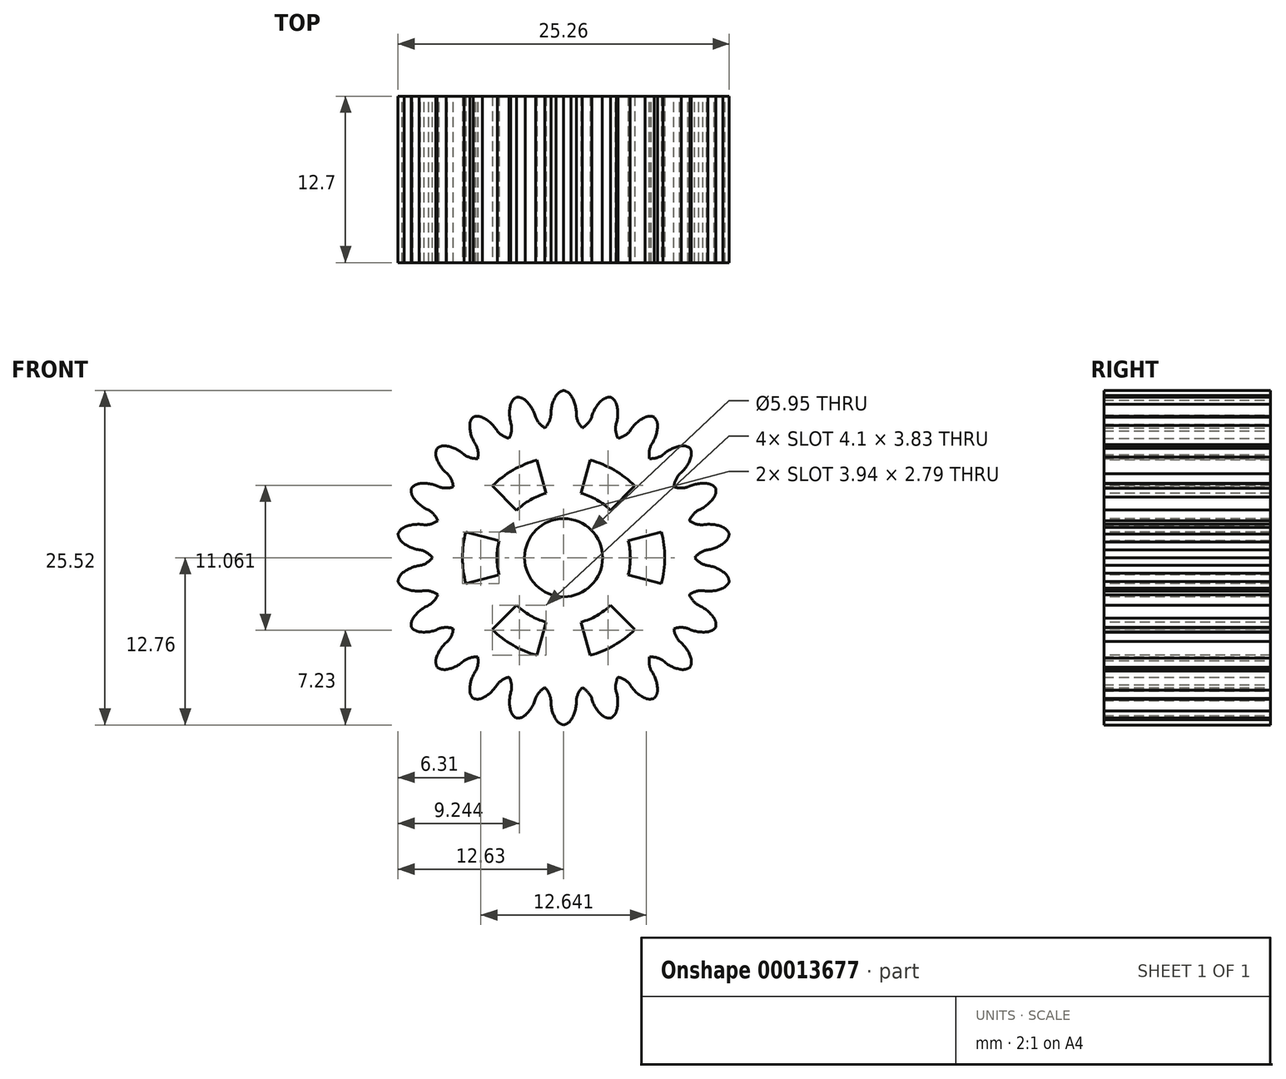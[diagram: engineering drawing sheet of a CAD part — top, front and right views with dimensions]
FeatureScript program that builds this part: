
annotation { "Feature Type Name" : "Feature", "Feature Type Description" : "" }
export const myFeature = defineFeature(function(context is Context, id is Id, definition is map)
    precondition{}
    {
        {
            var Q0;
            Q0=qCreatedBy(makeId("Front.planeOp"),FACE);
            var sketch = newSketch(context, id + "F0", { "sketchPlane" : qUnion([Q0])});
            skLineSegment(sketch, "E0", {"start": v(0, 0) * mm, "end": v(0, 16.94) * mm});
            skArc(sketch, "E1", {"start": v(0, 12.76) * mm, "mid": v(-0.32, 12.62) * mm, "end": v(-0.57, 12.37) * mm});
            skArc(sketch, "E2.MirrorCS", {"start": v(0, 12.76) * mm, "mid": v(0.32, 12.62) * mm, "end": v(0.57, 12.37) * mm});
            skArc(sketch, "E3", {"start": v(-0.57, 12.37) * mm, "mid": v(-0.88, 11.66) * mm, "end": v(-0.97, 10.89) * mm});
            skArc(sketch, "E4", {"start": v(-1.42, 9.9) * mm, "mid": v(-1.11, 10.36) * mm, "end": v(-0.97, 10.89) * mm});
            skArc(sketch, "E5.MirrorCS", {"start": v(1.42, 9.9) * mm, "mid": v(1.11, 10.36) * mm, "end": v(0.97, 10.89) * mm});
            skArc(sketch, "E6.MirrorCS", {"start": v(0.57, 12.37) * mm, "mid": v(0.88, 11.66) * mm, "end": v(0.97, 10.89) * mm});
            skPoint(sketch, "E7", {"position": v(0, 12.7) * mm});
            skPoint(sketch, "E8.MirrorCS.end.orphan", {"position": v(0.57, 12.37) * mm});
            skPoint(sketch, "E8.MirrorCS.start.orphan", {"position": v(0, 12.37) * mm});
            skPoint(sketch, "E9.1.0", {"position": v(-3.48, 11.87) * mm});
            skPoint(sketch, "E9.1.1", {"position": v(-2.94, 12.03) * mm});
            skArc(sketch, "E9.1.2", {"start": v(-2.94, 12.03) * mm, "mid": v(-2.44, 11.43) * mm, "end": v(-2.14, 10.72) * mm});
            skPoint(sketch, "E9.1.3", {"position": v(-3.58, 12.19) * mm});
            skArc(sketch, "E9.1.4", {"start": v(-4.03, 11.7) * mm, "mid": v(-4.13, 10.94) * mm, "end": v(-4, 10.17) * mm});
            skArc(sketch, "E9.1.5", {"start": v(-4.16, 9.1) * mm, "mid": v(-3.99, 9.62) * mm, "end": v(-4, 10.17) * mm});
            skArc(sketch, "E9.1.6", {"start": v(-1.42, 9.9) * mm, "mid": v(-1.85, 10.25) * mm, "end": v(-2.14, 10.72) * mm});
            skPoint(sketch, "E9.1.7", {"position": v(-3.48, 11.87) * mm});
            skArc(sketch, "E9.1.8", {"start": v(-3.6, 12.25) * mm, "mid": v(-3.87, 12.02) * mm, "end": v(-4.03, 11.7) * mm});
            skArc(sketch, "E9.1.9", {"start": v(-3.6, 12.25) * mm, "mid": v(-3.25, 12.2) * mm, "end": v(-2.94, 12.03) * mm});
            skPoint(sketch, "E9.2.0", {"position": v(-6.69, 10.4) * mm});
            skPoint(sketch, "E9.2.1", {"position": v(-6.2, 10.71) * mm});
            skArc(sketch, "E9.2.2", {"start": v(-6.2, 10.71) * mm, "mid": v(-5.56, 10.28) * mm, "end": v(-5.07, 9.68) * mm});
            skPoint(sketch, "E9.2.3", {"position": v(-6.87, 10.68) * mm});
            skArc(sketch, "E9.2.4", {"start": v(-7.17, 10.1) * mm, "mid": v(-7.04, 9.33) * mm, "end": v(-6.7, 8.63) * mm});
            skArc(sketch, "E9.2.5", {"start": v(-6.55, 7.56) * mm, "mid": v(-6.54, 8.11) * mm, "end": v(-6.7, 8.63) * mm});
            skArc(sketch, "E9.2.6", {"start": v(-4.16, 9.1) * mm, "mid": v(-4.66, 9.32) * mm, "end": v(-5.07, 9.68) * mm});
            skPoint(sketch, "E9.2.7", {"position": v(-6.69, 10.4) * mm});
            skArc(sketch, "E9.2.8", {"start": v(-6.9, 10.74) * mm, "mid": v(-7.1, 10.44) * mm, "end": v(-7.17, 10.1) * mm});
            skArc(sketch, "E9.2.9", {"start": v(-6.9, 10.74) * mm, "mid": v(-6.55, 10.8) * mm, "end": v(-6.2, 10.71) * mm});
            skPoint(sketch, "E9.3.0", {"position": v(-9.35, 8.1) * mm});
            skPoint(sketch, "E9.3.1", {"position": v(-8.97, 8.53) * mm});
            skArc(sketch, "E9.3.2", {"start": v(-8.97, 8.53) * mm, "mid": v(-8.23, 8.3) * mm, "end": v(-7.6, 7.86) * mm});
            skPoint(sketch, "E9.3.3", {"position": v(-9.6, 8.32) * mm});
            skArc(sketch, "E9.3.4", {"start": v(-9.72, 7.67) * mm, "mid": v(-9.39, 6.97) * mm, "end": v(-8.86, 6.4) * mm});
            skArc(sketch, "E9.3.5", {"start": v(-8.42, 5.41) * mm, "mid": v(-8.56, 5.94) * mm, "end": v(-8.86, 6.4) * mm});
            skArc(sketch, "E9.3.6", {"start": v(-6.55, 7.56) * mm, "mid": v(-7.1, 7.62) * mm, "end": v(-7.6, 7.86) * mm});
            skPoint(sketch, "E9.3.7", {"position": v(-9.35, 8.1) * mm});
            skArc(sketch, "E9.3.8", {"start": v(-9.65, 8.36) * mm, "mid": v(-9.75, 8.02) * mm, "end": v(-9.72, 7.67) * mm});
            skArc(sketch, "E9.3.9", {"start": v(-9.65, 8.36) * mm, "mid": v(-9.33, 8.5) * mm, "end": v(-8.97, 8.53) * mm});
            skPoint(sketch, "E9.4.0", {"position": v(-11.25, 5.14) * mm});
            skPoint(sketch, "E9.4.1", {"position": v(-11.01, 5.66) * mm});
            skArc(sketch, "E9.4.2", {"start": v(-11.01, 5.66) * mm, "mid": v(-10.24, 5.64) * mm, "end": v(-9.5, 5.4) * mm});
            skPoint(sketch, "E9.4.3", {"position": v(-11.55, 5.28) * mm});
            skArc(sketch, "E9.4.4", {"start": v(-11.49, 4.62) * mm, "mid": v(-10.97, 4.04) * mm, "end": v(-10.3, 3.64) * mm});
            skArc(sketch, "E9.4.5", {"start": v(-9.6, 2.82) * mm, "mid": v(-9.88, 3.3) * mm, "end": v(-10.3, 3.64) * mm});
            skArc(sketch, "E9.4.6", {"start": v(-8.42, 5.41) * mm, "mid": v(-8.96, 5.32) * mm, "end": v(-9.5, 5.4) * mm});
            skPoint(sketch, "E9.4.7", {"position": v(-11.25, 5.14) * mm});
            skArc(sketch, "E9.4.8", {"start": v(-11.6, 5.3) * mm, "mid": v(-11.61, 4.95) * mm, "end": v(-11.49, 4.62) * mm});
            skArc(sketch, "E9.4.9", {"start": v(-11.6, 5.3) * mm, "mid": v(-11.35, 5.54) * mm, "end": v(-11.01, 5.66) * mm});
            skPoint(sketch, "E9.5.0", {"position": v(-12.24, 1.76) * mm});
            skPoint(sketch, "E9.5.1", {"position": v(-12.16, 2.32) * mm});
            skArc(sketch, "E9.5.2", {"start": v(-12.16, 2.32) * mm, "mid": v(-11.41, 2.53) * mm, "end": v(-10.64, 2.5) * mm});
            skPoint(sketch, "E9.5.3", {"position": v(-12.57, 1.8) * mm});
            skArc(sketch, "E9.5.4", {"start": v(-12.32, 1.2) * mm, "mid": v(-11.66, 0.79) * mm, "end": v(-10.91, 0.59) * mm});
            skArc(sketch, "E9.5.5", {"start": v(-10, 0) * mm, "mid": v(-10.41, 0.37) * mm, "end": v(-10.91, 0.59) * mm});
            skArc(sketch, "E9.5.6", {"start": v(-9.6, 2.82) * mm, "mid": v(-10.1, 2.58) * mm, "end": v(-10.64, 2.5) * mm});
            skPoint(sketch, "E9.5.7", {"position": v(-12.24, 1.76) * mm});
            skArc(sketch, "E9.5.8", {"start": v(-12.63, 1.82) * mm, "mid": v(-12.54, 1.48) * mm, "end": v(-12.32, 1.2) * mm});
            skArc(sketch, "E9.5.9", {"start": v(-12.63, 1.82) * mm, "mid": v(-12.45, 2.12) * mm, "end": v(-12.16, 2.32) * mm});
            skPoint(sketch, "E9.6.0", {"position": v(-12.24, -1.76) * mm});
            skPoint(sketch, "E9.6.1", {"position": v(-12.32, -1.2) * mm});
            skArc(sketch, "E9.6.2", {"start": v(-12.32, -1.2) * mm, "mid": v(-11.66, -0.79) * mm, "end": v(-10.91, -0.59) * mm});
            skPoint(sketch, "E9.6.3", {"position": v(-12.57, -1.8) * mm});
            skArc(sketch, "E9.6.4", {"start": v(-12.16, -2.32) * mm, "mid": v(-11.41, -2.53) * mm, "end": v(-10.64, -2.5) * mm});
            skArc(sketch, "E9.6.5", {"start": v(-9.6, -2.82) * mm, "mid": v(-10.1, -2.58) * mm, "end": v(-10.64, -2.5) * mm});
            skArc(sketch, "E9.6.6", {"start": v(-10, 0) * mm, "mid": v(-10.41, -0.37) * mm, "end": v(-10.91, -0.59) * mm});
            skPoint(sketch, "E9.6.7", {"position": v(-12.24, -1.76) * mm});
            skArc(sketch, "E9.6.8", {"start": v(-12.63, -1.82) * mm, "mid": v(-12.45, -2.12) * mm, "end": v(-12.16, -2.32) * mm});
            skArc(sketch, "E9.6.9", {"start": v(-12.63, -1.82) * mm, "mid": v(-12.54, -1.48) * mm, "end": v(-12.32, -1.2) * mm});
            skPoint(sketch, "E9.7.0", {"position": v(-11.25, -5.14) * mm});
            skPoint(sketch, "E9.7.1", {"position": v(-11.49, -4.62) * mm});
            skArc(sketch, "E9.7.2", {"start": v(-11.49, -4.62) * mm, "mid": v(-10.97, -4.04) * mm, "end": v(-10.3, -3.64) * mm});
            skPoint(sketch, "E9.7.3", {"position": v(-11.55, -5.28) * mm});
            skArc(sketch, "E9.7.4", {"start": v(-11.01, -5.66) * mm, "mid": v(-10.24, -5.64) * mm, "end": v(-9.5, -5.4) * mm});
            skArc(sketch, "E9.7.5", {"start": v(-8.42, -5.41) * mm, "mid": v(-8.96, -5.32) * mm, "end": v(-9.5, -5.4) * mm});
            skArc(sketch, "E9.7.6", {"start": v(-9.6, -2.82) * mm, "mid": v(-9.88, -3.3) * mm, "end": v(-10.3, -3.64) * mm});
            skPoint(sketch, "E9.7.7", {"position": v(-11.25, -5.14) * mm});
            skArc(sketch, "E9.7.8", {"start": v(-11.6, -5.3) * mm, "mid": v(-11.35, -5.54) * mm, "end": v(-11.01, -5.66) * mm});
            skArc(sketch, "E9.7.9", {"start": v(-11.6, -5.3) * mm, "mid": v(-11.61, -4.95) * mm, "end": v(-11.49, -4.62) * mm});
            skPoint(sketch, "E9.8.0", {"position": v(-9.35, -8.1) * mm});
            skPoint(sketch, "E9.8.1", {"position": v(-9.72, -7.67) * mm});
            skArc(sketch, "E9.8.2", {"start": v(-9.72, -7.67) * mm, "mid": v(-9.39, -6.97) * mm, "end": v(-8.86, -6.4) * mm});
            skPoint(sketch, "E9.8.3", {"position": v(-9.6, -8.32) * mm});
            skArc(sketch, "E9.8.4", {"start": v(-8.97, -8.53) * mm, "mid": v(-8.23, -8.3) * mm, "end": v(-7.6, -7.86) * mm});
            skArc(sketch, "E9.8.5", {"start": v(-6.55, -7.56) * mm, "mid": v(-7.1, -7.62) * mm, "end": v(-7.6, -7.86) * mm});
            skArc(sketch, "E9.8.6", {"start": v(-8.42, -5.41) * mm, "mid": v(-8.56, -5.94) * mm, "end": v(-8.86, -6.4) * mm});
            skPoint(sketch, "E9.8.7", {"position": v(-9.35, -8.1) * mm});
            skArc(sketch, "E9.8.8", {"start": v(-9.65, -8.36) * mm, "mid": v(-9.33, -8.5) * mm, "end": v(-8.97, -8.53) * mm});
            skArc(sketch, "E9.8.9", {"start": v(-9.65, -8.36) * mm, "mid": v(-9.75, -8.02) * mm, "end": v(-9.72, -7.67) * mm});
            skPoint(sketch, "E9.9.0", {"position": v(-6.69, -10.4) * mm});
            skPoint(sketch, "E9.9.1", {"position": v(-7.17, -10.1) * mm});
            skArc(sketch, "E9.9.2", {"start": v(-7.17, -10.1) * mm, "mid": v(-7.04, -9.33) * mm, "end": v(-6.7, -8.63) * mm});
            skPoint(sketch, "E9.9.3", {"position": v(-6.87, -10.68) * mm});
            skArc(sketch, "E9.9.4", {"start": v(-6.2, -10.71) * mm, "mid": v(-5.56, -10.28) * mm, "end": v(-5.07, -9.68) * mm});
            skArc(sketch, "E9.9.5", {"start": v(-4.16, -9.1) * mm, "mid": v(-4.66, -9.32) * mm, "end": v(-5.07, -9.68) * mm});
            skArc(sketch, "E9.9.6", {"start": v(-6.55, -7.56) * mm, "mid": v(-6.54, -8.11) * mm, "end": v(-6.7, -8.63) * mm});
            skPoint(sketch, "E9.9.7", {"position": v(-6.69, -10.4) * mm});
            skArc(sketch, "E9.9.8", {"start": v(-6.9, -10.74) * mm, "mid": v(-6.55, -10.8) * mm, "end": v(-6.2, -10.71) * mm});
            skArc(sketch, "E9.9.9", {"start": v(-6.9, -10.74) * mm, "mid": v(-7.1, -10.44) * mm, "end": v(-7.17, -10.1) * mm});
            skPoint(sketch, "E9.10.0", {"position": v(-3.48, -11.87) * mm});
            skPoint(sketch, "E9.10.1", {"position": v(-4.03, -11.7) * mm});
            skArc(sketch, "E9.10.2", {"start": v(-4.03, -11.7) * mm, "mid": v(-4.13, -10.94) * mm, "end": v(-4, -10.17) * mm});
            skPoint(sketch, "E9.10.3", {"position": v(-3.58, -12.19) * mm});
            skArc(sketch, "E9.10.4", {"start": v(-2.94, -12.03) * mm, "mid": v(-2.44, -11.43) * mm, "end": v(-2.14, -10.72) * mm});
            skArc(sketch, "E9.10.5", {"start": v(-1.42, -9.9) * mm, "mid": v(-1.85, -10.25) * mm, "end": v(-2.14, -10.72) * mm});
            skArc(sketch, "E9.10.6", {"start": v(-4.16, -9.1) * mm, "mid": v(-3.99, -9.62) * mm, "end": v(-4, -10.17) * mm});
            skPoint(sketch, "E9.10.7", {"position": v(-3.48, -11.87) * mm});
            skArc(sketch, "E9.10.8", {"start": v(-3.6, -12.25) * mm, "mid": v(-3.25, -12.2) * mm, "end": v(-2.94, -12.03) * mm});
            skArc(sketch, "E9.10.9", {"start": v(-3.6, -12.25) * mm, "mid": v(-3.87, -12.02) * mm, "end": v(-4.03, -11.7) * mm});
            skPoint(sketch, "E9.11.0", {"position": v(0, -12.37) * mm});
            skPoint(sketch, "E9.11.1", {"position": v(-0.57, -12.37) * mm});
            skArc(sketch, "E9.11.2", {"start": v(-0.57, -12.37) * mm, "mid": v(-0.88, -11.66) * mm, "end": v(-0.97, -10.89) * mm});
            skPoint(sketch, "E9.11.3", {"position": v(0, -12.7) * mm});
            skArc(sketch, "E9.11.4", {"start": v(0.57, -12.37) * mm, "mid": v(0.88, -11.66) * mm, "end": v(0.97, -10.89) * mm});
            skArc(sketch, "E9.11.5", {"start": v(1.42, -9.9) * mm, "mid": v(1.11, -10.36) * mm, "end": v(0.97, -10.89) * mm});
            skArc(sketch, "E9.11.6", {"start": v(-1.42, -9.9) * mm, "mid": v(-1.11, -10.36) * mm, "end": v(-0.97, -10.89) * mm});
            skPoint(sketch, "E9.11.7", {"position": v(0, -12.37) * mm});
            skArc(sketch, "E9.11.8", {"start": v(0, -12.76) * mm, "mid": v(0.32, -12.62) * mm, "end": v(0.57, -12.37) * mm});
            skArc(sketch, "E9.11.9", {"start": v(0, -12.76) * mm, "mid": v(-0.32, -12.62) * mm, "end": v(-0.57, -12.37) * mm});
            skPoint(sketch, "E9.12.0", {"position": v(3.48, -11.87) * mm});
            skPoint(sketch, "E9.12.1", {"position": v(2.94, -12.03) * mm});
            skArc(sketch, "E9.12.2", {"start": v(2.94, -12.03) * mm, "mid": v(2.44, -11.43) * mm, "end": v(2.14, -10.72) * mm});
            skPoint(sketch, "E9.12.3", {"position": v(3.58, -12.19) * mm});
            skArc(sketch, "E9.12.4", {"start": v(4.03, -11.7) * mm, "mid": v(4.13, -10.94) * mm, "end": v(4, -10.17) * mm});
            skArc(sketch, "E9.12.5", {"start": v(4.16, -9.1) * mm, "mid": v(3.99, -9.62) * mm, "end": v(4, -10.17) * mm});
            skArc(sketch, "E9.12.6", {"start": v(1.42, -9.9) * mm, "mid": v(1.85, -10.25) * mm, "end": v(2.14, -10.72) * mm});
            skPoint(sketch, "E9.12.7", {"position": v(3.48, -11.87) * mm});
            skArc(sketch, "E9.12.8", {"start": v(3.6, -12.25) * mm, "mid": v(3.87, -12.02) * mm, "end": v(4.03, -11.7) * mm});
            skArc(sketch, "E9.12.9", {"start": v(3.6, -12.25) * mm, "mid": v(3.25, -12.2) * mm, "end": v(2.94, -12.03) * mm});
            skPoint(sketch, "E9.13.0", {"position": v(6.69, -10.4) * mm});
            skPoint(sketch, "E9.13.1", {"position": v(6.2, -10.71) * mm});
            skArc(sketch, "E9.13.2", {"start": v(6.2, -10.71) * mm, "mid": v(5.56, -10.28) * mm, "end": v(5.07, -9.68) * mm});
            skPoint(sketch, "E9.13.3", {"position": v(6.87, -10.68) * mm});
            skArc(sketch, "E9.13.4", {"start": v(7.17, -10.1) * mm, "mid": v(7.04, -9.33) * mm, "end": v(6.7, -8.63) * mm});
            skArc(sketch, "E9.13.5", {"start": v(6.55, -7.56) * mm, "mid": v(6.54, -8.11) * mm, "end": v(6.7, -8.63) * mm});
            skArc(sketch, "E9.13.6", {"start": v(4.16, -9.1) * mm, "mid": v(4.66, -9.32) * mm, "end": v(5.07, -9.68) * mm});
            skPoint(sketch, "E9.13.7", {"position": v(6.69, -10.4) * mm});
            skArc(sketch, "E9.13.8", {"start": v(6.9, -10.74) * mm, "mid": v(7.1, -10.44) * mm, "end": v(7.17, -10.1) * mm});
            skArc(sketch, "E9.13.9", {"start": v(6.9, -10.74) * mm, "mid": v(6.55, -10.8) * mm, "end": v(6.2, -10.71) * mm});
            skPoint(sketch, "E9.14.0", {"position": v(9.35, -8.1) * mm});
            skPoint(sketch, "E9.14.1", {"position": v(8.97, -8.53) * mm});
            skArc(sketch, "E9.14.2", {"start": v(8.97, -8.53) * mm, "mid": v(8.23, -8.3) * mm, "end": v(7.6, -7.86) * mm});
            skPoint(sketch, "E9.14.3", {"position": v(9.6, -8.32) * mm});
            skArc(sketch, "E9.14.4", {"start": v(9.72, -7.67) * mm, "mid": v(9.39, -6.97) * mm, "end": v(8.86, -6.4) * mm});
            skArc(sketch, "E9.14.5", {"start": v(8.42, -5.41) * mm, "mid": v(8.56, -5.94) * mm, "end": v(8.86, -6.4) * mm});
            skArc(sketch, "E9.14.6", {"start": v(6.55, -7.56) * mm, "mid": v(7.1, -7.62) * mm, "end": v(7.6, -7.86) * mm});
            skPoint(sketch, "E9.14.7", {"position": v(9.35, -8.1) * mm});
            skArc(sketch, "E9.14.8", {"start": v(9.65, -8.36) * mm, "mid": v(9.75, -8.02) * mm, "end": v(9.72, -7.67) * mm});
            skArc(sketch, "E9.14.9", {"start": v(9.65, -8.36) * mm, "mid": v(9.33, -8.5) * mm, "end": v(8.97, -8.53) * mm});
            skPoint(sketch, "E9.15.0", {"position": v(11.25, -5.14) * mm});
            skPoint(sketch, "E9.15.1", {"position": v(11.01, -5.66) * mm});
            skArc(sketch, "E9.15.2", {"start": v(11.01, -5.66) * mm, "mid": v(10.24, -5.64) * mm, "end": v(9.5, -5.4) * mm});
            skPoint(sketch, "E9.15.3", {"position": v(11.55, -5.28) * mm});
            skArc(sketch, "E9.15.4", {"start": v(11.49, -4.62) * mm, "mid": v(10.97, -4.04) * mm, "end": v(10.3, -3.64) * mm});
            skArc(sketch, "E9.15.5", {"start": v(9.6, -2.82) * mm, "mid": v(9.88, -3.3) * mm, "end": v(10.3, -3.64) * mm});
            skArc(sketch, "E9.15.6", {"start": v(8.42, -5.41) * mm, "mid": v(8.96, -5.32) * mm, "end": v(9.5, -5.4) * mm});
            skPoint(sketch, "E9.15.7", {"position": v(11.25, -5.14) * mm});
            skArc(sketch, "E9.15.8", {"start": v(11.6, -5.3) * mm, "mid": v(11.61, -4.95) * mm, "end": v(11.49, -4.62) * mm});
            skArc(sketch, "E9.15.9", {"start": v(11.6, -5.3) * mm, "mid": v(11.35, -5.54) * mm, "end": v(11.01, -5.66) * mm});
            skPoint(sketch, "E9.16.0", {"position": v(12.24, -1.76) * mm});
            skPoint(sketch, "E9.16.1", {"position": v(12.16, -2.32) * mm});
            skArc(sketch, "E9.16.2", {"start": v(12.16, -2.32) * mm, "mid": v(11.41, -2.53) * mm, "end": v(10.64, -2.5) * mm});
            skPoint(sketch, "E9.16.3", {"position": v(12.57, -1.8) * mm});
            skArc(sketch, "E9.16.4", {"start": v(12.32, -1.2) * mm, "mid": v(11.66, -0.79) * mm, "end": v(10.91, -0.59) * mm});
            skArc(sketch, "E9.16.5", {"start": v(10, 0) * mm, "mid": v(10.41, -0.37) * mm, "end": v(10.91, -0.59) * mm});
            skArc(sketch, "E9.16.6", {"start": v(9.6, -2.82) * mm, "mid": v(10.1, -2.58) * mm, "end": v(10.64, -2.5) * mm});
            skPoint(sketch, "E9.16.7", {"position": v(12.24, -1.76) * mm});
            skArc(sketch, "E9.16.8", {"start": v(12.63, -1.82) * mm, "mid": v(12.54, -1.48) * mm, "end": v(12.32, -1.2) * mm});
            skArc(sketch, "E9.16.9", {"start": v(12.63, -1.82) * mm, "mid": v(12.45, -2.12) * mm, "end": v(12.16, -2.32) * mm});
            skPoint(sketch, "E9.17.0", {"position": v(12.24, 1.76) * mm});
            skPoint(sketch, "E9.17.1", {"position": v(12.32, 1.2) * mm});
            skArc(sketch, "E9.17.2", {"start": v(12.32, 1.2) * mm, "mid": v(11.66, 0.79) * mm, "end": v(10.91, 0.59) * mm});
            skPoint(sketch, "E9.17.3", {"position": v(12.57, 1.8) * mm});
            skArc(sketch, "E9.17.4", {"start": v(12.16, 2.32) * mm, "mid": v(11.41, 2.53) * mm, "end": v(10.64, 2.5) * mm});
            skArc(sketch, "E9.17.5", {"start": v(9.6, 2.82) * mm, "mid": v(10.1, 2.58) * mm, "end": v(10.64, 2.5) * mm});
            skArc(sketch, "E9.17.6", {"start": v(10, 0) * mm, "mid": v(10.41, 0.37) * mm, "end": v(10.91, 0.59) * mm});
            skPoint(sketch, "E9.17.7", {"position": v(12.24, 1.76) * mm});
            skArc(sketch, "E9.17.8", {"start": v(12.63, 1.82) * mm, "mid": v(12.45, 2.12) * mm, "end": v(12.16, 2.32) * mm});
            skArc(sketch, "E9.17.9", {"start": v(12.63, 1.82) * mm, "mid": v(12.54, 1.48) * mm, "end": v(12.32, 1.2) * mm});
            skPoint(sketch, "E9.18.0", {"position": v(11.25, 5.14) * mm});
            skPoint(sketch, "E9.18.1", {"position": v(11.49, 4.62) * mm});
            skArc(sketch, "E9.18.2", {"start": v(11.49, 4.62) * mm, "mid": v(10.97, 4.04) * mm, "end": v(10.3, 3.64) * mm});
            skPoint(sketch, "E9.18.3", {"position": v(11.55, 5.28) * mm});
            skArc(sketch, "E9.18.4", {"start": v(11.01, 5.66) * mm, "mid": v(10.24, 5.64) * mm, "end": v(9.5, 5.4) * mm});
            skArc(sketch, "E9.18.5", {"start": v(8.42, 5.41) * mm, "mid": v(8.96, 5.32) * mm, "end": v(9.5, 5.4) * mm});
            skArc(sketch, "E9.18.6", {"start": v(9.6, 2.82) * mm, "mid": v(9.88, 3.3) * mm, "end": v(10.3, 3.64) * mm});
            skPoint(sketch, "E9.18.7", {"position": v(11.25, 5.14) * mm});
            skArc(sketch, "E9.18.8", {"start": v(11.6, 5.3) * mm, "mid": v(11.35, 5.54) * mm, "end": v(11.01, 5.66) * mm});
            skArc(sketch, "E9.18.9", {"start": v(11.6, 5.3) * mm, "mid": v(11.61, 4.95) * mm, "end": v(11.49, 4.62) * mm});
            skPoint(sketch, "E9.19.0", {"position": v(9.35, 8.1) * mm});
            skPoint(sketch, "E9.19.1", {"position": v(9.72, 7.67) * mm});
            skArc(sketch, "E9.19.2", {"start": v(9.72, 7.67) * mm, "mid": v(9.39, 6.97) * mm, "end": v(8.86, 6.4) * mm});
            skPoint(sketch, "E9.19.3", {"position": v(9.6, 8.32) * mm});
            skArc(sketch, "E9.19.4", {"start": v(8.97, 8.53) * mm, "mid": v(8.23, 8.3) * mm, "end": v(7.6, 7.86) * mm});
            skArc(sketch, "E9.19.5", {"start": v(6.55, 7.56) * mm, "mid": v(7.1, 7.62) * mm, "end": v(7.6, 7.86) * mm});
            skArc(sketch, "E9.19.6", {"start": v(8.42, 5.41) * mm, "mid": v(8.56, 5.94) * mm, "end": v(8.86, 6.4) * mm});
            skPoint(sketch, "E9.19.7", {"position": v(9.35, 8.1) * mm});
            skArc(sketch, "E9.19.8", {"start": v(9.65, 8.36) * mm, "mid": v(9.33, 8.5) * mm, "end": v(8.97, 8.53) * mm});
            skArc(sketch, "E9.19.9", {"start": v(9.65, 8.36) * mm, "mid": v(9.75, 8.02) * mm, "end": v(9.72, 7.67) * mm});
            skPoint(sketch, "E9.20.0", {"position": v(6.69, 10.4) * mm});
            skPoint(sketch, "E9.20.1", {"position": v(7.17, 10.1) * mm});
            skArc(sketch, "E9.20.2", {"start": v(7.17, 10.1) * mm, "mid": v(7.04, 9.33) * mm, "end": v(6.7, 8.63) * mm});
            skPoint(sketch, "E9.20.3", {"position": v(6.87, 10.68) * mm});
            skArc(sketch, "E9.20.4", {"start": v(6.2, 10.71) * mm, "mid": v(5.56, 10.28) * mm, "end": v(5.07, 9.68) * mm});
            skArc(sketch, "E9.20.5", {"start": v(4.16, 9.1) * mm, "mid": v(4.66, 9.32) * mm, "end": v(5.07, 9.68) * mm});
            skArc(sketch, "E9.20.6", {"start": v(6.55, 7.56) * mm, "mid": v(6.54, 8.11) * mm, "end": v(6.7, 8.63) * mm});
            skPoint(sketch, "E9.20.7", {"position": v(6.69, 10.4) * mm});
            skArc(sketch, "E9.20.8", {"start": v(6.9, 10.74) * mm, "mid": v(6.55, 10.8) * mm, "end": v(6.2, 10.71) * mm});
            skArc(sketch, "E9.20.9", {"start": v(6.9, 10.74) * mm, "mid": v(7.1, 10.44) * mm, "end": v(7.17, 10.1) * mm});
            skPoint(sketch, "E9.21.0", {"position": v(3.48, 11.87) * mm});
            skPoint(sketch, "E9.21.1", {"position": v(4.03, 11.7) * mm});
            skArc(sketch, "E9.21.2", {"start": v(4.03, 11.7) * mm, "mid": v(4.13, 10.94) * mm, "end": v(4, 10.17) * mm});
            skPoint(sketch, "E9.21.3", {"position": v(3.58, 12.19) * mm});
            skArc(sketch, "E9.21.4", {"start": v(2.94, 12.03) * mm, "mid": v(2.44, 11.43) * mm, "end": v(2.14, 10.72) * mm});
            skArc(sketch, "E9.21.5", {"start": v(1.42, 9.9) * mm, "mid": v(1.85, 10.25) * mm, "end": v(2.14, 10.72) * mm});
            skArc(sketch, "E9.21.6", {"start": v(4.16, 9.1) * mm, "mid": v(3.99, 9.62) * mm, "end": v(4, 10.17) * mm});
            skPoint(sketch, "E9.21.7", {"position": v(3.48, 11.87) * mm});
            skArc(sketch, "E9.21.8", {"start": v(3.6, 12.25) * mm, "mid": v(3.25, 12.2) * mm, "end": v(2.94, 12.03) * mm});
            skArc(sketch, "E9.21.9", {"start": v(3.6, 12.25) * mm, "mid": v(3.87, 12.02) * mm, "end": v(4.03, 11.7) * mm});
            skPoint(sketch, "E9.center", {"position": v(0, 0) * mm});
            skPoint(sketch, "E10.orphan", {"position": v(-1.54, 9.8) * mm});
            skPoint(sketch, "E11.orphan", {"position": v(-1.29, 9.84) * mm});
            skPoint(sketch, "E12.orphan", {"position": v(1.54, 9.8) * mm});
            skPoint(sketch, "E13.orphan", {"position": v(1.29, 9.84) * mm});
            skPoint(sketch, "E14.orphan", {"position": v(4, 9.08) * mm});
            skPoint(sketch, "E15.orphan", {"position": v(4.24, 8.97) * mm});
            skPoint(sketch, "E16.orphan", {"position": v(6.4, 7.58) * mm});
            skPoint(sketch, "E17.orphan", {"position": v(6.6, 7.42) * mm});
            skPoint(sketch, "E18.orphan", {"position": v(8.28, 5.47) * mm});
            skPoint(sketch, "E19.orphan", {"position": v(8.41, 5.26) * mm});
            skPoint(sketch, "E20.orphan", {"position": v(9.56, 2.67) * mm});
            skPoint(sketch, "E21.orphan", {"position": v(9.92, -0.13) * mm});
            skPoint(sketch, "E22.orphan", {"position": v(9.56, -2.67) * mm});
            skPoint(sketch, "E23.orphan", {"position": v(9.48, -2.92) * mm});
            skPoint(sketch, "E24.orphan", {"position": v(8.28, -5.47) * mm});
            skPoint(sketch, "E25.orphan", {"position": v(6.6, -7.42) * mm});
            skPoint(sketch, "E26.orphan", {"position": v(6.4, -7.58) * mm});
            skPoint(sketch, "E27.orphan", {"position": v(4.24, -8.97) * mm});
            skPoint(sketch, "E28.orphan", {"position": v(4, -9.08) * mm});
            skPoint(sketch, "E29.orphan", {"position": v(1.29, -9.84) * mm});
            skPoint(sketch, "E30.orphan", {"position": v(1.54, -9.8) * mm});
            skPoint(sketch, "E31.orphan", {"position": v(-1.29, -9.84) * mm});
            skPoint(sketch, "E32.orphan", {"position": v(-1.54, -9.8) * mm});
            skPoint(sketch, "E33.orphan", {"position": v(-4, -9.08) * mm});
            skPoint(sketch, "E34.orphan", {"position": v(-4.24, -8.97) * mm});
            skPoint(sketch, "E35.orphan", {"position": v(-6.4, -7.58) * mm});
            skPoint(sketch, "E36.orphan", {"position": v(-6.6, -7.42) * mm});
            skPoint(sketch, "E37.orphan", {"position": v(-8.41, -5.26) * mm});
            skPoint(sketch, "E38.orphan", {"position": v(-8.28, -5.47) * mm});
            skPoint(sketch, "E39.orphan", {"position": v(-9.56, -2.67) * mm});
            skPoint(sketch, "E40.orphan", {"position": v(-9.48, -2.92) * mm});
            skPoint(sketch, "E41.orphan", {"position": v(-9.92, -0.13) * mm});
            skPoint(sketch, "E42.orphan", {"position": v(-9.92, 0.13) * mm});
            skPoint(sketch, "E43.orphan", {"position": v(-9.56, 2.67) * mm});
            skPoint(sketch, "E44.orphan", {"position": v(-9.48, 2.92) * mm});
            skPoint(sketch, "E45.orphan", {"position": v(-8.41, 5.26) * mm});
            skPoint(sketch, "E46.orphan", {"position": v(-8.28, 5.47) * mm});
            skPoint(sketch, "E47.orphan", {"position": v(-6.6, 7.42) * mm});
            skPoint(sketch, "E48.orphan", {"position": v(-6.4, 7.58) * mm});
            skPoint(sketch, "E49.orphan", {"position": v(-4.24, 8.97) * mm});
            skPoint(sketch, "E50.orphan", {"position": v(-4, 9.08) * mm});
            skSolve(sketch);
        }
        {
            var Q0;
            Q0=makeQuery(id+"F0.imprint","IMPRINT",FACE,{"disambiguationData":[TD([[makeQuery(id+"F0.imprint","IMPRINT",EDGE,{"derivedFrom":sQuery(id+"F0.wireOp",EDGE,"E1")}),1.0]])]});
            extrude(context, id + "F1", {"entities" : qUnion([Q0]), "depth" : 12.7 * mm});
        }
        {
            var Q0;
            Q0=makeQuery(id+"F1.opExtrude","CAP_FACE",FACE,{"disambiguationData":[OSD([sQuery(id+"F0.wireOp",EDGE,"E1"),sQuery(id+"F0.wireOp",EDGE,"E2.MirrorCS"),sQuery(id+"F0.wireOp",EDGE,"E3"),sQuery(id+"F0.wireOp",EDGE,"E4"),sQuery(id+"F0.wireOp",EDGE,"E5.MirrorCS"),sQuery(id+"F0.wireOp",EDGE,"E6.MirrorCS"),sQuery(id+"F0.wireOp",EDGE,"E9.1.2"),sQuery(id+"F0.wireOp",EDGE,"E9.1.4"),sQuery(id+"F0.wireOp",EDGE,"E9.1.5"),sQuery(id+"F0.wireOp",EDGE,"E9.1.6"),sQuery(id+"F0.wireOp",EDGE,"E9.1.8"),sQuery(id+"F0.wireOp",EDGE,"E9.1.9"),sQuery(id+"F0.wireOp",EDGE,"E9.2.2"),sQuery(id+"F0.wireOp",EDGE,"E9.2.4"),sQuery(id+"F0.wireOp",EDGE,"E9.2.5"),sQuery(id+"F0.wireOp",EDGE,"E9.2.6"),sQuery(id+"F0.wireOp",EDGE,"E9.2.8"),sQuery(id+"F0.wireOp",EDGE,"E9.2.9"),sQuery(id+"F0.wireOp",EDGE,"E9.3.2"),sQuery(id+"F0.wireOp",EDGE,"E9.3.4"),sQuery(id+"F0.wireOp",EDGE,"E9.3.5"),sQuery(id+"F0.wireOp",EDGE,"E9.3.6"),sQuery(id+"F0.wireOp",EDGE,"E9.3.8"),sQuery(id+"F0.wireOp",EDGE,"E9.3.9"),sQuery(id+"F0.wireOp",EDGE,"E9.4.2"),sQuery(id+"F0.wireOp",EDGE,"E9.4.4"),sQuery(id+"F0.wireOp",EDGE,"E9.4.5"),sQuery(id+"F0.wireOp",EDGE,"E9.4.6"),sQuery(id+"F0.wireOp",EDGE,"E9.4.8"),sQuery(id+"F0.wireOp",EDGE,"E9.4.9"),sQuery(id+"F0.wireOp",EDGE,"E9.5.2"),sQuery(id+"F0.wireOp",EDGE,"E9.5.4"),sQuery(id+"F0.wireOp",EDGE,"E9.5.5"),sQuery(id+"F0.wireOp",EDGE,"E9.5.6"),sQuery(id+"F0.wireOp",EDGE,"E9.5.8"),sQuery(id+"F0.wireOp",EDGE,"E9.5.9"),sQuery(id+"F0.wireOp",EDGE,"E9.6.2"),sQuery(id+"F0.wireOp",EDGE,"E9.6.4"),sQuery(id+"F0.wireOp",EDGE,"E9.6.5"),sQuery(id+"F0.wireOp",EDGE,"E9.6.6"),sQuery(id+"F0.wireOp",EDGE,"E9.6.8"),sQuery(id+"F0.wireOp",EDGE,"E9.6.9"),sQuery(id+"F0.wireOp",EDGE,"E9.7.2"),sQuery(id+"F0.wireOp",EDGE,"E9.7.4"),sQuery(id+"F0.wireOp",EDGE,"E9.7.5"),sQuery(id+"F0.wireOp",EDGE,"E9.7.6"),sQuery(id+"F0.wireOp",EDGE,"E9.7.8"),sQuery(id+"F0.wireOp",EDGE,"E9.7.9"),sQuery(id+"F0.wireOp",EDGE,"E9.8.2"),sQuery(id+"F0.wireOp",EDGE,"E9.8.4"),sQuery(id+"F0.wireOp",EDGE,"E9.8.5"),sQuery(id+"F0.wireOp",EDGE,"E9.8.6"),sQuery(id+"F0.wireOp",EDGE,"E9.8.8"),sQuery(id+"F0.wireOp",EDGE,"E9.8.9"),sQuery(id+"F0.wireOp",EDGE,"E9.9.2"),sQuery(id+"F0.wireOp",EDGE,"E9.9.4"),sQuery(id+"F0.wireOp",EDGE,"E9.9.5"),sQuery(id+"F0.wireOp",EDGE,"E9.9.6"),sQuery(id+"F0.wireOp",EDGE,"E9.9.8"),sQuery(id+"F0.wireOp",EDGE,"E9.9.9"),sQuery(id+"F0.wireOp",EDGE,"E9.10.2"),sQuery(id+"F0.wireOp",EDGE,"E9.10.4"),sQuery(id+"F0.wireOp",EDGE,"E9.10.5"),sQuery(id+"F0.wireOp",EDGE,"E9.10.6"),sQuery(id+"F0.wireOp",EDGE,"E9.10.8"),sQuery(id+"F0.wireOp",EDGE,"E9.10.9"),sQuery(id+"F0.wireOp",EDGE,"E9.11.2"),sQuery(id+"F0.wireOp",EDGE,"E9.11.4"),sQuery(id+"F0.wireOp",EDGE,"E9.11.5"),sQuery(id+"F0.wireOp",EDGE,"E9.11.6"),sQuery(id+"F0.wireOp",EDGE,"E9.11.8"),sQuery(id+"F0.wireOp",EDGE,"E9.11.9"),sQuery(id+"F0.wireOp",EDGE,"E9.12.2"),sQuery(id+"F0.wireOp",EDGE,"E9.12.4"),sQuery(id+"F0.wireOp",EDGE,"E9.12.5"),sQuery(id+"F0.wireOp",EDGE,"E9.12.6"),sQuery(id+"F0.wireOp",EDGE,"E9.12.8"),sQuery(id+"F0.wireOp",EDGE,"E9.12.9"),sQuery(id+"F0.wireOp",EDGE,"E9.13.2"),sQuery(id+"F0.wireOp",EDGE,"E9.13.4"),sQuery(id+"F0.wireOp",EDGE,"E9.13.5"),sQuery(id+"F0.wireOp",EDGE,"E9.13.6"),sQuery(id+"F0.wireOp",EDGE,"E9.13.8"),sQuery(id+"F0.wireOp",EDGE,"E9.13.9"),sQuery(id+"F0.wireOp",EDGE,"E9.14.2"),sQuery(id+"F0.wireOp",EDGE,"E9.14.4"),sQuery(id+"F0.wireOp",EDGE,"E9.14.5"),sQuery(id+"F0.wireOp",EDGE,"E9.14.6"),sQuery(id+"F0.wireOp",EDGE,"E9.14.8"),sQuery(id+"F0.wireOp",EDGE,"E9.14.9"),sQuery(id+"F0.wireOp",EDGE,"E9.15.2"),sQuery(id+"F0.wireOp",EDGE,"E9.15.4"),sQuery(id+"F0.wireOp",EDGE,"E9.15.5"),sQuery(id+"F0.wireOp",EDGE,"E9.15.6"),sQuery(id+"F0.wireOp",EDGE,"E9.15.8"),sQuery(id+"F0.wireOp",EDGE,"E9.15.9"),sQuery(id+"F0.wireOp",EDGE,"E9.16.2"),sQuery(id+"F0.wireOp",EDGE,"E9.16.4"),sQuery(id+"F0.wireOp",EDGE,"E9.16.5"),sQuery(id+"F0.wireOp",EDGE,"E9.16.6"),sQuery(id+"F0.wireOp",EDGE,"E9.16.8"),sQuery(id+"F0.wireOp",EDGE,"E9.16.9"),sQuery(id+"F0.wireOp",EDGE,"E9.17.2"),sQuery(id+"F0.wireOp",EDGE,"E9.17.4"),sQuery(id+"F0.wireOp",EDGE,"E9.17.5"),sQuery(id+"F0.wireOp",EDGE,"E9.17.6"),sQuery(id+"F0.wireOp",EDGE,"E9.17.8"),sQuery(id+"F0.wireOp",EDGE,"E9.17.9"),sQuery(id+"F0.wireOp",EDGE,"E9.18.2"),sQuery(id+"F0.wireOp",EDGE,"E9.18.4"),sQuery(id+"F0.wireOp",EDGE,"E9.18.5"),sQuery(id+"F0.wireOp",EDGE,"E9.18.6"),sQuery(id+"F0.wireOp",EDGE,"E9.18.8"),sQuery(id+"F0.wireOp",EDGE,"E9.18.9"),sQuery(id+"F0.wireOp",EDGE,"E9.19.2"),sQuery(id+"F0.wireOp",EDGE,"E9.19.4"),sQuery(id+"F0.wireOp",EDGE,"E9.19.5"),sQuery(id+"F0.wireOp",EDGE,"E9.19.6"),sQuery(id+"F0.wireOp",EDGE,"E9.19.8"),sQuery(id+"F0.wireOp",EDGE,"E9.19.9"),sQuery(id+"F0.wireOp",EDGE,"E9.20.2"),sQuery(id+"F0.wireOp",EDGE,"E9.20.4"),sQuery(id+"F0.wireOp",EDGE,"E9.20.5"),sQuery(id+"F0.wireOp",EDGE,"E9.20.6"),sQuery(id+"F0.wireOp",EDGE,"E9.20.8"),sQuery(id+"F0.wireOp",EDGE,"E9.20.9"),sQuery(id+"F0.wireOp",EDGE,"E9.21.2"),sQuery(id+"F0.wireOp",EDGE,"E9.21.4"),sQuery(id+"F0.wireOp",EDGE,"E9.21.5"),sQuery(id+"F0.wireOp",EDGE,"E9.21.6"),sQuery(id+"F0.wireOp",EDGE,"E9.21.8"),sQuery(id+"F0.wireOp",EDGE,"E9.21.9")])],"isStart":false});
            var sketch = newSketch(context, id + "F2", { "sketchPlane" : qUnion([Q0])});
            skCircle(sketch, "E51", {"center": v(0, 0) * mm, "radius": 2.98 * mm});
            skArc(sketch, "E52", {"start": v(-1.34, 4.91) * mm, "mid": v(-2.55, 4.4) * mm, "end": v(-3.59, 3.61) * mm});
            skArc(sketch, "E53", {"start": v(-2.03, 7.45) * mm, "mid": v(-3.86, 6.68) * mm, "end": v(-5.44, 5.48) * mm});
            skLineSegment(sketch, "E54", {"start": v(-3.59, 3.61) * mm, "end": v(-5.44, 5.48) * mm});
            skPoint(sketch, "E55.orphan", {"position": v(-6.3, 6.35) * mm});
            skPoint(sketch, "E56.orphan", {"position": v(-2.35, 8.63) * mm});
            skLineSegment(sketch, "E57.trimOffspring", {"start": v(-1.34, 4.91) * mm, "end": v(-2.03, 7.45) * mm});
            skArc(sketch, "E58.1.0", {"start": v(-4.92, 1.3) * mm, "mid": v(-5.1, 0) * mm, "end": v(-4.92, -1.3) * mm});
            skLineSegment(sketch, "E58.1.1", {"start": v(-4.92, -1.3) * mm, "end": v(-7.46, -1.97) * mm});
            skLineSegment(sketch, "E58.1.2", {"start": v(-4.92, 1.3) * mm, "end": v(-7.46, 1.97) * mm});
            skPoint(sketch, "E58.1.3", {"position": v(-8.65, -2.28) * mm});
            skArc(sketch, "E58.1.4", {"start": v(-7.46, 1.97) * mm, "mid": v(-7.72, 0) * mm, "end": v(-7.46, -1.97) * mm});
            skPoint(sketch, "E58.1.5", {"position": v(-8.65, 2.28) * mm});
            skArc(sketch, "E58.2.0", {"start": v(-3.59, -3.61) * mm, "mid": v(-2.55, -4.4) * mm, "end": v(-1.34, -4.91) * mm});
            skLineSegment(sketch, "E58.2.1", {"start": v(-1.34, -4.91) * mm, "end": v(-2.03, -7.45) * mm});
            skLineSegment(sketch, "E58.2.2", {"start": v(-3.59, -3.61) * mm, "end": v(-5.44, -5.48) * mm});
            skPoint(sketch, "E58.2.3", {"position": v(-2.35, -8.63) * mm});
            skArc(sketch, "E58.2.4", {"start": v(-5.44, -5.48) * mm, "mid": v(-3.86, -6.68) * mm, "end": v(-2.03, -7.45) * mm});
            skPoint(sketch, "E58.2.5", {"position": v(-6.3, -6.35) * mm});
            skArc(sketch, "E58.3.0", {"start": v(1.34, -4.91) * mm, "mid": v(2.55, -4.4) * mm, "end": v(3.59, -3.61) * mm});
            skLineSegment(sketch, "E58.3.1", {"start": v(3.59, -3.61) * mm, "end": v(5.44, -5.48) * mm});
            skLineSegment(sketch, "E58.3.2", {"start": v(1.34, -4.91) * mm, "end": v(2.03, -7.45) * mm});
            skPoint(sketch, "E58.3.3", {"position": v(6.3, -6.35) * mm});
            skArc(sketch, "E58.3.4", {"start": v(2.03, -7.45) * mm, "mid": v(3.86, -6.68) * mm, "end": v(5.44, -5.48) * mm});
            skPoint(sketch, "E58.3.5", {"position": v(2.35, -8.63) * mm});
            skArc(sketch, "E58.4.0", {"start": v(4.92, -1.3) * mm, "mid": v(5.1, 0) * mm, "end": v(4.92, 1.3) * mm});
            skLineSegment(sketch, "E58.4.1", {"start": v(4.92, 1.3) * mm, "end": v(7.46, 1.97) * mm});
            skLineSegment(sketch, "E58.4.2", {"start": v(4.92, -1.3) * mm, "end": v(7.46, -1.97) * mm});
            skPoint(sketch, "E58.4.3", {"position": v(8.65, 2.28) * mm});
            skArc(sketch, "E58.4.4", {"start": v(7.46, -1.97) * mm, "mid": v(7.72, 0) * mm, "end": v(7.46, 1.97) * mm});
            skPoint(sketch, "E58.4.5", {"position": v(8.65, -2.28) * mm});
            skArc(sketch, "E58.5.0", {"start": v(3.59, 3.61) * mm, "mid": v(2.55, 4.4) * mm, "end": v(1.34, 4.91) * mm});
            skLineSegment(sketch, "E58.5.1", {"start": v(1.34, 4.91) * mm, "end": v(2.03, 7.45) * mm});
            skLineSegment(sketch, "E58.5.2", {"start": v(3.59, 3.61) * mm, "end": v(5.44, 5.48) * mm});
            skPoint(sketch, "E58.5.3", {"position": v(2.35, 8.63) * mm});
            skArc(sketch, "E58.5.4", {"start": v(5.44, 5.48) * mm, "mid": v(3.86, 6.68) * mm, "end": v(2.03, 7.45) * mm});
            skPoint(sketch, "E58.5.5", {"position": v(6.3, 6.35) * mm});
            skSolve(sketch);
        }
        {
            var Q0;
            Q0=makeQuery(id+"F2.imprint","IMPRINT",FACE,{"disambiguationData":[TD([[makeQuery(id+"F2.imprint","IMPRINT",EDGE,{"derivedFrom":sQuery(id+"F2.wireOp",EDGE,"E52")}),-1.0]])]});
            var Q1;
            Q1=makeQuery(id+"F2.imprint","IMPRINT",FACE,{"disambiguationData":[TD([[makeQuery(id+"F2.imprint","IMPRINT",EDGE,{"derivedFrom":sQuery(id+"F2.wireOp",EDGE,"E58.5.0")}),-1.0]])]});
            var Q2;
            Q2=makeQuery(id+"F2.imprint","IMPRINT",FACE,{"disambiguationData":[TD([[makeQuery(id+"F2.imprint","IMPRINT",EDGE,{"derivedFrom":sQuery(id+"F2.wireOp",EDGE,"E58.4.0")}),-1.0]])]});
            var Q3;
            Q3=makeQuery(id+"F2.imprint","IMPRINT",FACE,{"disambiguationData":[TD([[makeQuery(id+"F2.imprint","IMPRINT",EDGE,{"derivedFrom":sQuery(id+"F2.wireOp",EDGE,"E58.3.0")}),-1.0]])]});
            var Q4;
            Q4=makeQuery(id+"F2.imprint","IMPRINT",FACE,{"disambiguationData":[TD([[makeQuery(id+"F2.imprint","IMPRINT",EDGE,{"derivedFrom":sQuery(id+"F2.wireOp",EDGE,"E58.2.0")}),-1.0]])]});
            var Q5;
            Q5=makeQuery(id+"F2.imprint","IMPRINT",FACE,{"disambiguationData":[TD([[makeQuery(id+"F2.imprint","IMPRINT",EDGE,{"derivedFrom":sQuery(id+"F2.wireOp",EDGE,"E58.1.0")}),-1.0]])]});
            var Q6;
            Q6=makeQuery(id+"F2.imprint","IMPRINT",FACE,{"disambiguationData":[TD([[makeQuery(id+"F2.imprint","IMPRINT",EDGE,{"derivedFrom":sQuery(id+"F2.wireOp",EDGE,"E51")}),1.0]])]});
            extrude(context, id + "F3", {"entities" : qUnion([Q0, Q1, Q2, Q3, Q4, Q5, Q6]), "operationType" : NewBodyOperationType.REMOVE, "oppositeDirection" : true, "depth" : 25.4 * mm});
        }
    });
